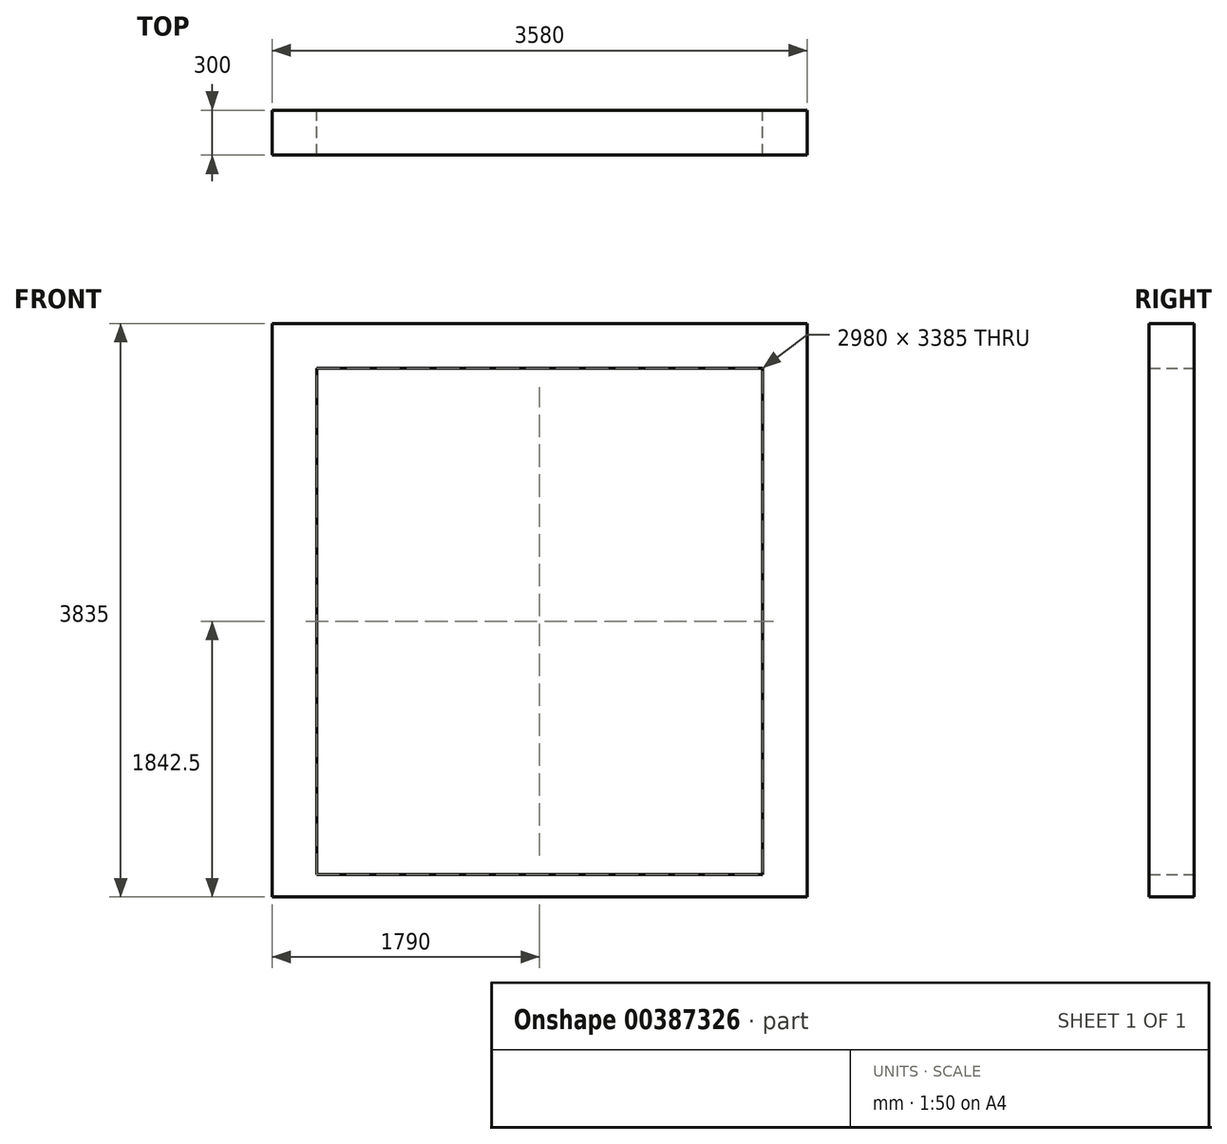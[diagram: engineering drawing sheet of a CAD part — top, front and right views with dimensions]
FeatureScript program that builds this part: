
annotation { "Feature Type Name" : "Feature", "Feature Type Description" : "" }
export const myFeature = defineFeature(function(context is Context, id is Id, definition is map)
    precondition{}
    {
        {
            var Q0;
            Q0=qCreatedBy(makeId("Front.planeOp"),FACE);
            var sketch = newSketch(context, id + "F0", { "sketchPlane" : qUnion([Q0])});
            skLineSegment(sketch, "E0.bottom", {"start": v(300, 3535) * mm, "end": v(3280, 3535) * mm});
            skLineSegment(sketch, "E0.top", {"start": v(300, 150) * mm, "end": v(3280, 150) * mm});
            skLineSegment(sketch, "E0.left", {"start": v(300, 3535) * mm, "end": v(300, 150) * mm});
            skLineSegment(sketch, "E0.right", {"start": v(3280, 3535) * mm, "end": v(3280, 150) * mm});
            skLineSegment(sketch, "E1.bottom", {"start": v(0, 3835) * mm, "end": v(3580, 3835) * mm});
            skLineSegment(sketch, "E1.top", {"start": v(0, 150) * mm, "end": v(3580, 150) * mm});
            skLineSegment(sketch, "E1.left", {"start": v(0, 3835) * mm, "end": v(0, 150) * mm});
            skLineSegment(sketch, "E1.right", {"start": v(3580, 3835) * mm, "end": v(3580, 150) * mm});
            skLineSegment(sketch, "E2", {"start": v(1790, 3535) * mm, "end": v(1790, 150) * mm, "construction": true});
            skLineSegment(sketch, "E3.top", {"start": v(0, 0) * mm, "end": v(3580, 0) * mm});
            skLineSegment(sketch, "E3.left", {"start": v(0, 150) * mm, "end": v(0, 0) * mm});
            skLineSegment(sketch, "E3.right", {"start": v(3580, 150) * mm, "end": v(3580, 0) * mm});
            skSolve(sketch);
        }
        {
            var Q0;
            Q0=makeQuery(id+"F0.imprint","IMPRINT",FACE,{"disambiguationData":[TD([[makeQuery(id+"F0.imprint","IMPRINT",EDGE,{"derivedFrom":sQuery(id+"F0.wireOp",EDGE,"E0.bottom")}),1.0]])]});
            var Q1;
            Q1=makeQuery(id+"F0.imprint","IMPRINT",FACE,{"disambiguationData":[TD([[makeQuery(id+"F0.imprint","IMPRINT",EDGE,{"derivedFrom":sQuery(id+"F0.wireOp",EDGE,"E3.top")}),1.0]])]});
            extrude(context, id + "F1", {"entities" : qUnion([Q0, Q1]), "depth" : 300 * mm, "offsetDistance" : 25 * mm});
        }
        {
            var Q0;
            Q0=makeQuery(id+"F1.opExtrude","SWEPT_FACE",FACE,{"disambiguationData":[OSD([sQuery(id+"F0.wireOp",EDGE,"E0.left")])]});
            var sketch = newSketch(context, id + "F2", { "sketchPlane" : qUnion([Q0])});
            skLineSegment(sketch, "E4", {"start": v(-225, 3535) * mm, "end": v(-225, 150) * mm, "construction": true});
            skPoint(sketch, "E5", {"position": v(-225, 790) * mm});
            skPoint(sketch, "E6", {"position": v(-225, 2505) * mm});
            skSolve(sketch);
        }
        {
            var Q0;
            Q0=makeQuery(id+"F1.opExtrude","SWEPT_FACE",FACE,{"disambiguationData":[OSD([sQuery(id+"F0.wireOp",EDGE,"E0.right")])]});
            var sketch = newSketch(context, id + "F3", { "sketchPlane" : qUnion([Q0])});
            skLineSegment(sketch, "E7.0", {"start": v(225, 3535) * mm, "end": v(225, 150) * mm, "construction": true});
            skPoint(sketch, "E8.0", {"position": v(225, 790) * mm});
            skPoint(sketch, "E9.0", {"position": v(225, 2505) * mm});
            skSolve(sketch);
        }
    });
